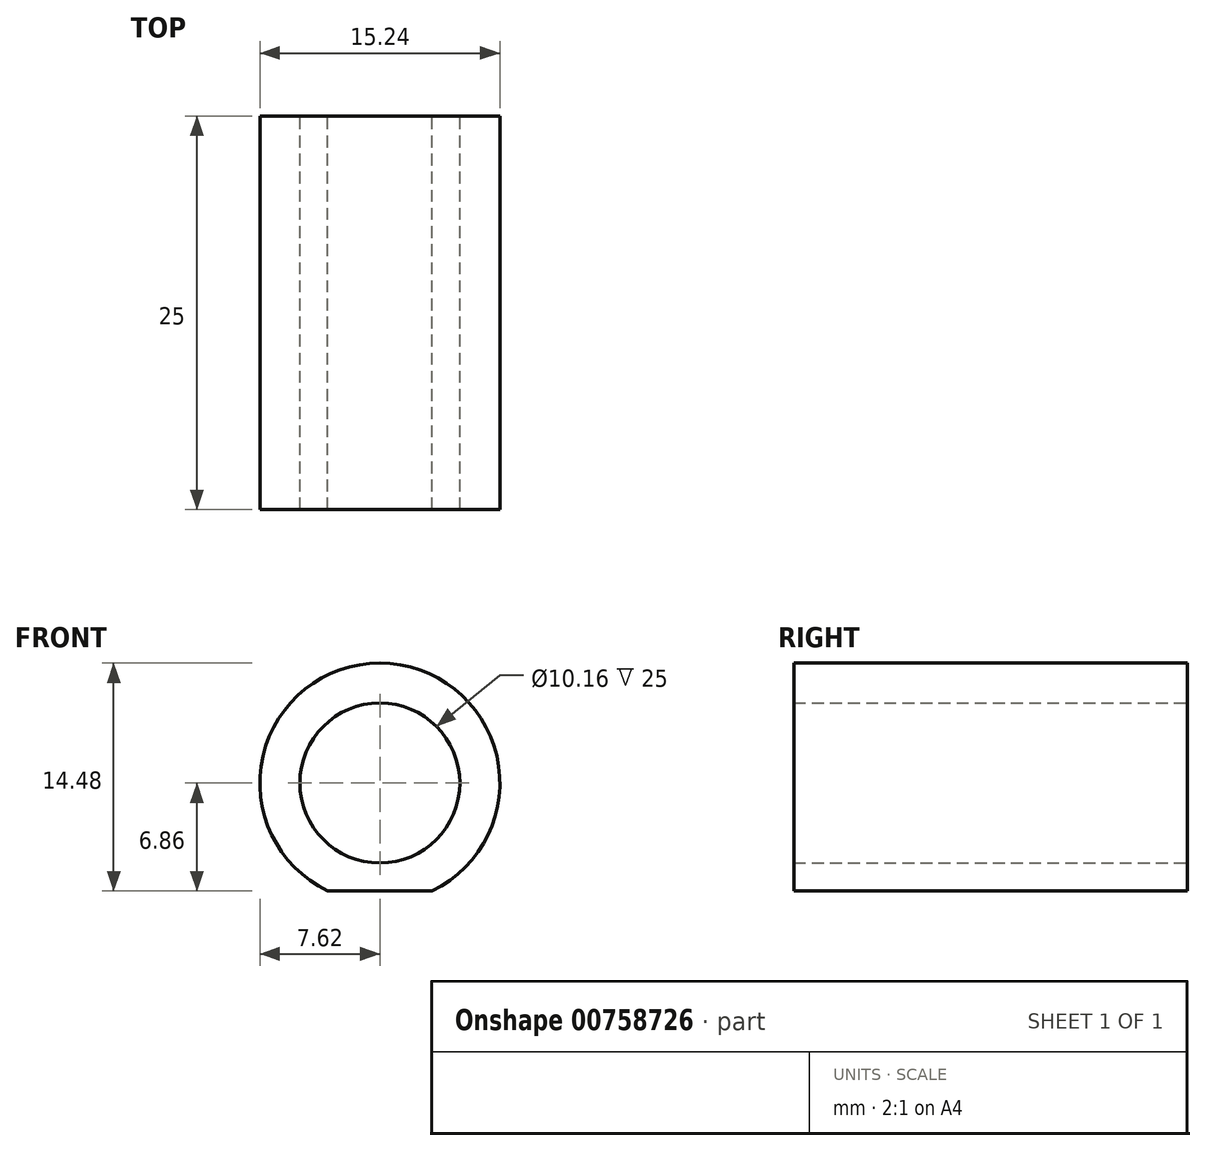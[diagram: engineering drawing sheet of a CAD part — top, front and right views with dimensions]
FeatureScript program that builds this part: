
annotation { "Feature Type Name" : "Feature", "Feature Type Description" : "" }
export const myFeature = defineFeature(function(context is Context, id is Id, definition is map)
    precondition{}
    {
        {
            var Q0;
            Q0=qCreatedBy(makeId("Front.planeOp"),FACE);
            var sketch = newSketch(context, id + "F0", { "sketchPlane" : qUnion([Q0])});
            skCircle(sketch, "E0", {"center": v(0, 0) * mm, "radius": 5.08 * mm});
            skCircle(sketch, "E1", {"center": v(0, 0) * mm, "radius": 7.62 * mm});
            skLineSegment(sketch, "E2", {"start": v(0, 0) * mm, "end": v(0, -10.16) * mm});
            skSolve(sketch);
        }
        {
            var Q0;
            Q0=makeQuery(id+"F0.imprint","IMPRINT",FACE,{"disambiguationData":[TD([[makeQuery(id+"F0.imprint","IMPRINT",EDGE,{"derivedFrom":sQuery(id+"F0.wireOp",EDGE,"E0")}),-1.0]])]});
            extrude(context, id + "F1", {"entities" : qUnion([Q0]), "depth" : 25 * mm, "offsetDistance" : 25.4 * mm});
        }
        {
            var Q0;
            Q0=qCreatedBy(makeId("Front.planeOp"),FACE);
            var sketch = newSketch(context, id + "F2", { "sketchPlane" : qUnion([Q0])});
            skLineSegment(sketch, "E3", {"start": v(0, 0) * mm, "end": v(0, -10.16) * mm});
            skLineSegment(sketch, "E4", {"start": v(0, -10.16) * mm, "end": v(0, -6.86) * mm});
            skLineSegment(sketch, "E5", {"start": v(0, -6.86) * mm, "end": v(-7.23, -6.86) * mm});
            skLineSegment(sketch, "E6", {"start": v(-7.23, -6.86) * mm, "end": v(-7.23, -10.16) * mm});
            skLineSegment(sketch, "E7", {"start": v(-7.23, -10.16) * mm, "end": v(7.63, -10.16) * mm});
            skLineSegment(sketch, "E8", {"start": v(7.63, -10.16) * mm, "end": v(7.63, -6.86) * mm});
            skLineSegment(sketch, "E9", {"start": v(7.63, -6.86) * mm, "end": v(0, -6.86) * mm});
            skSolve(sketch);
        }
        {
            var Q0;
            {var subQ4=sQuery(id+"F2.wireOp",EDGE,"E8");Q0=makeQuery(id+"F2.imprint","IMPRINT",FACE,{"disambiguationData":[TD([[makeQuery(id+"F2.imprint","IMPRINT",EDGE,{"derivedFrom":subQ4}),1.0]])]});}
            var Q1;
            {var subQ3=sQuery(id+"F2.wireOp",EDGE,"E5");Q1=makeQuery(id+"F2.imprint","IMPRINT",FACE,{"disambiguationData":[TD([[makeQuery(id+"F2.imprint","IMPRINT",EDGE,{"derivedFrom":subQ3}),1.0]])]});}
            extrude(context, id + "F3", {"entities" : qUnion([Q0, Q1]), "operationType" : NewBodyOperationType.REMOVE, "depth" : 181.1 * mm, "offsetDistance" : 25.4 * mm});
        }
    });
